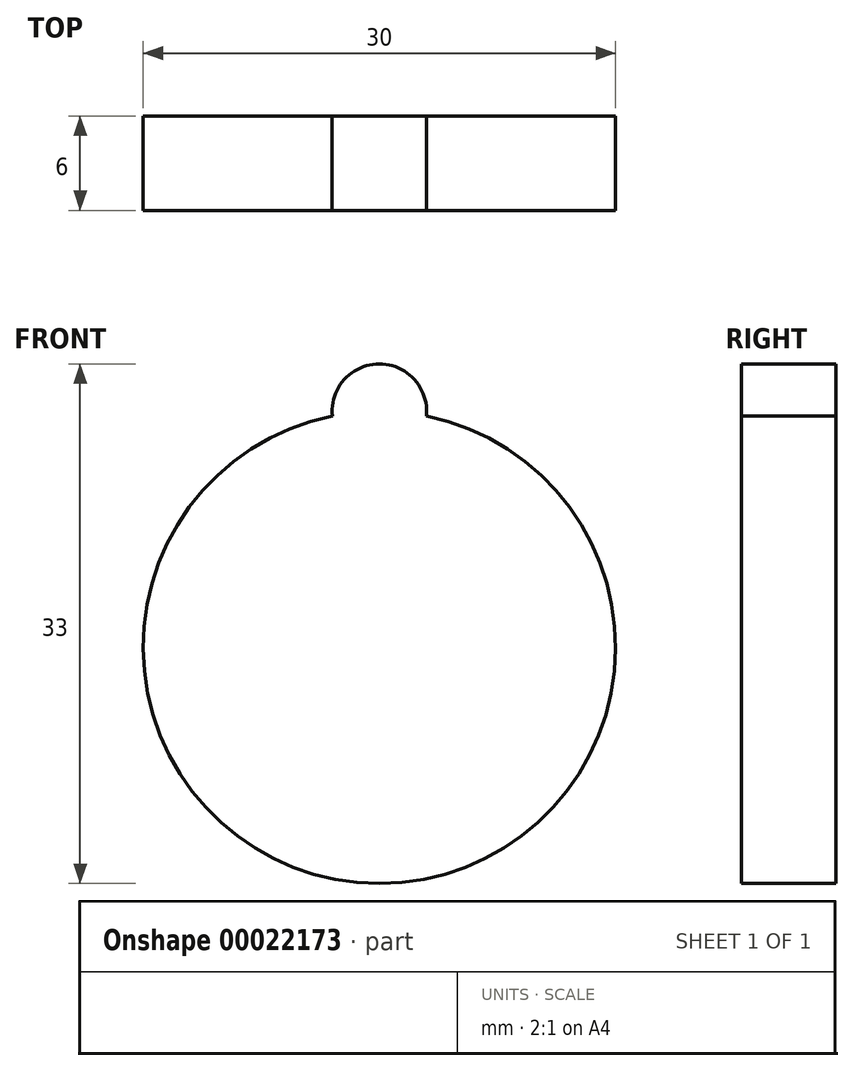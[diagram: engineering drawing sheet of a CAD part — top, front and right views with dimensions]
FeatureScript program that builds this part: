
annotation { "Feature Type Name" : "Feature", "Feature Type Description" : "" }
export const myFeature = defineFeature(function(context is Context, id is Id, definition is map)
    precondition{}
    {
        {
            var Q0;
            Q0=qCreatedBy(makeId("Front.planeOp"),FACE);
            var sketch = newSketch(context, id + "F0", { "sketchPlane" : qUnion([Q0])});
            skCircle(sketch, "E0", {"center": v(0, 0) * mm, "radius": 15 * mm});
            skCircle(sketch, "E1", {"center": v(0, 15) * mm, "radius": 3 * mm});
            skSolve(sketch);
        }
        {
            var Q0;
            Q0 = qSketchRegion(id + "F0", true);
            extrude(context, id + "F1", {"entities" : qUnion([Q0]), "depth" : 6 * mm});
        }
    });
